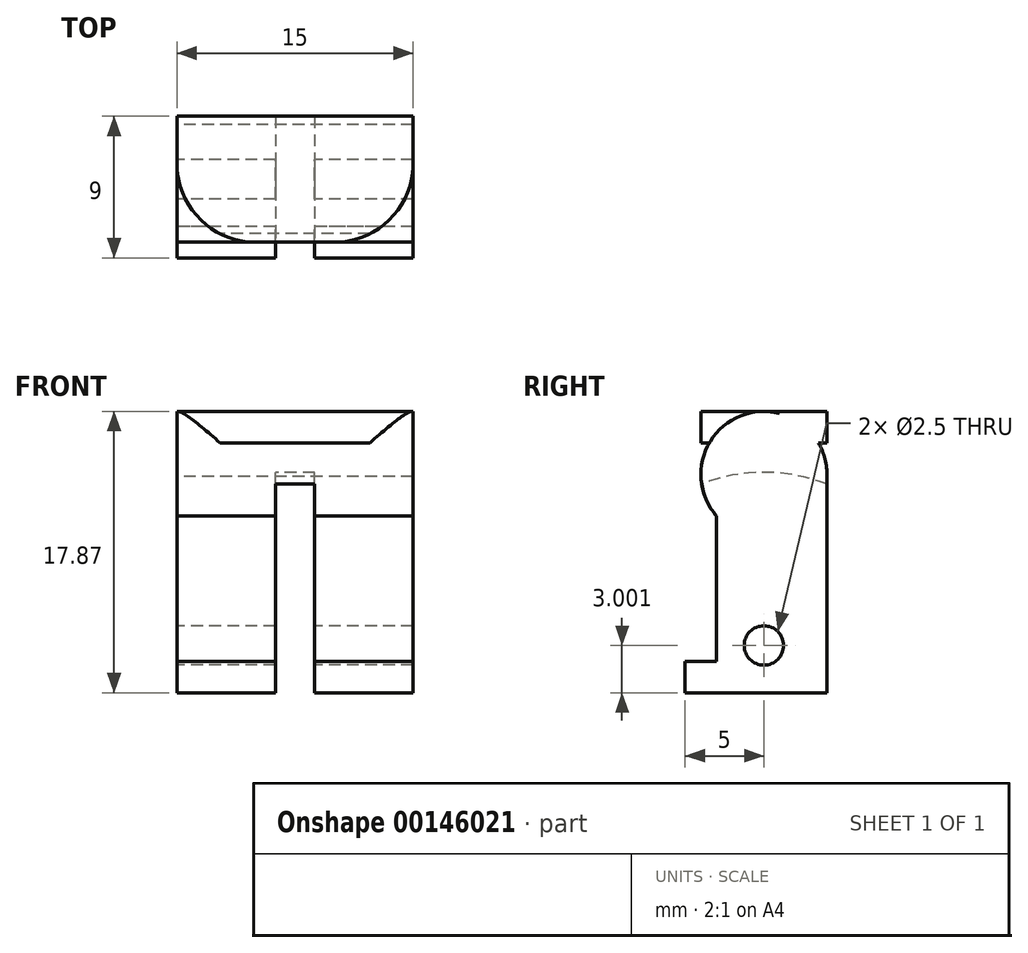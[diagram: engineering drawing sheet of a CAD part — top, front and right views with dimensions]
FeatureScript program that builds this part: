
annotation { "Feature Type Name" : "Feature", "Feature Type Description" : "" }
export const myFeature = defineFeature(function(context is Context, id is Id, definition is map)
    precondition{}
    {
        {
            var Q0;
            Q0=qCreatedBy(makeId("Right.planeOp"),FACE);
            var sketch = newSketch(context, id + "F0", { "sketchPlane" : qUnion([Q0])});
            skLineSegment(sketch, "E0.bottom", {"start": v(4, 1) * mm, "end": v(-4, 1) * mm});
            skLineSegment(sketch, "E0.top", {"start": v(4, -1) * mm, "end": v(3.46, -1) * mm});
            skLineSegment(sketch, "E0.left", {"start": v(4, 1) * mm, "end": v(4, -1) * mm});
            skLineSegment(sketch, "E0.right", {"start": v(-4, 1) * mm, "end": v(-4, -1) * mm});
            skPoint(sketch, "E0.middle", {"position": v(0, 0) * mm});
            skArc(sketch, "E1", {"start": v(-3.46, -1) * mm, "mid": v(-3.98, -3.4) * mm, "end": v(-3, -5.64) * mm});
            skLineSegment(sketch, "E2.left", {"start": v(4, -14.87) * mm, "end": v(4, -2.87) * mm});
            skLineSegment(sketch, "E2.right", {"start": v(-3, -14.87) * mm, "end": v(-3, -5.64) * mm});
            skLineSegment(sketch, "E3.top", {"start": v(4, -16.87) * mm, "end": v(-5, -16.87) * mm});
            skLineSegment(sketch, "E3.left", {"start": v(4, -14.87) * mm, "end": v(4, -16.87) * mm});
            skLineSegment(sketch, "E3.right", {"start": v(-5, -14.87) * mm, "end": v(-5, -16.87) * mm});
            skCircle(sketch, "E4", {"center": v(0, -13.87) * mm, "radius": 1.25 * mm});
            skLineSegment(sketch, "E5.trimOffspring", {"start": v(-3.46, -1) * mm, "end": v(-4, -1) * mm});
            skArc(sketch, "E6.trimOffspring", {"start": v(4, -3.13) * mm, "mid": v(3.88, -2.03) * mm, "end": v(3.46, -1) * mm});
            skLineSegment(sketch, "E7.trimOffspring", {"start": v(-3, -14.87) * mm, "end": v(-5, -14.87) * mm});
            skSolve(sketch);
        }
        {
            var Q0;
            Q0=qSketchRegion(id+"F0",true);
            extrude(context, id + "F1", {"entities" : qUnion([Q0]), "endBound" : BoundingType.SYMMETRIC, "depth" : 15 * mm});
        }
        {
            var Q0;
            Q0=qCreatedBy(makeId("Right.planeOp"),FACE);
            var sketch = newSketch(context, id + "F2", { "sketchPlane" : qUnion([Q0])});
            skCircle(sketch, "E8", {"center": v(0, -13.87) * mm, "radius": 11 * mm});
            skSolve(sketch);
        }
        {
            var Q0;
            Q0=qSketchRegion(id+"F2",true);
            extrude(context, id + "F3", {"entities" : qUnion([Q0]), "operationType" : NewBodyOperationType.REMOVE, "endBound" : BoundingType.SYMMETRIC, "depth" : 2.5 * mm});
        }
        {
            var Q0;
            Q0=makeQuery(id+"F1.opExtrude","CAP_EDGE",EDGE,{"disambiguationData":[OSD([sQuery(id+"F0.wireOp",EDGE,"E0.right")])],"isStart":false});
            var Q1;
            Q1=makeQuery(id+"F1.opExtrude","CAP_EDGE",EDGE,{"disambiguationData":[OSD([sQuery(id+"F0.wireOp",EDGE,"E0.right")])],"isStart":true});
            fillet(context, id + "F4", {"entities" : qUnion([Q0, Q1]), "radius" : 5 * mm, "tangentPropagation" : true, "allowEdgeOverflow" : false});
        }
    });
